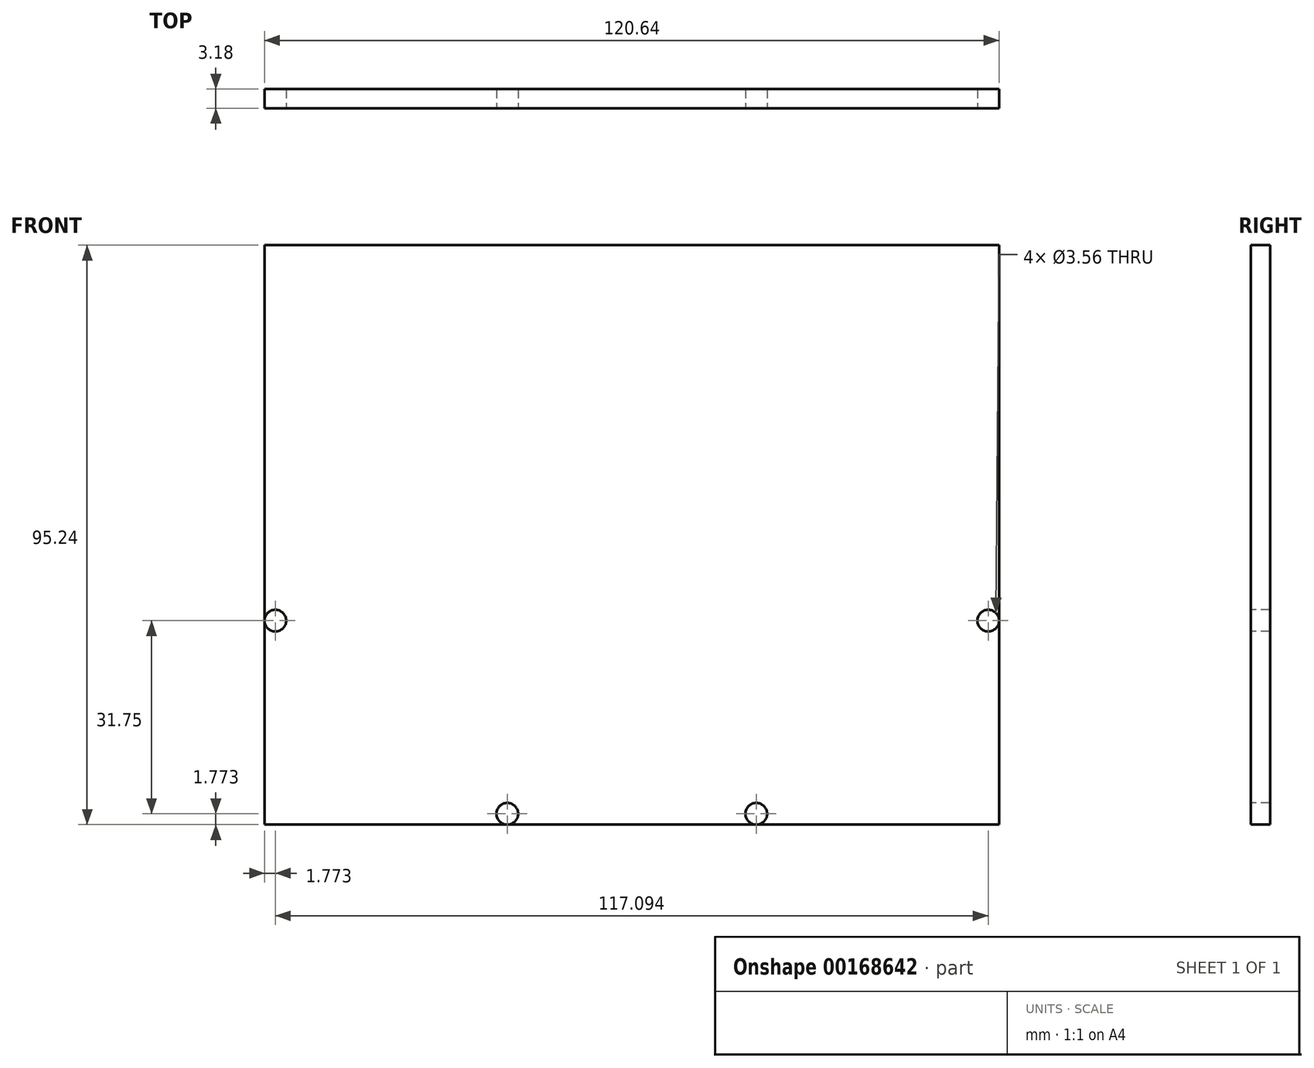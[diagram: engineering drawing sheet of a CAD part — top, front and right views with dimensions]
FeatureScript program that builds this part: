
annotation { "Feature Type Name" : "Feature", "Feature Type Description" : "" }
export const myFeature = defineFeature(function(context is Context, id is Id, definition is map)
    precondition{}
    {
        {
            var Q0;
            Q0=qCreatedBy(makeId("Front.planeOp"),FACE);
            var sketch = newSketch(context, id + "F0", { "sketchPlane" : qUnion([Q0])});
            skLineSegment(sketch, "E0.bottom", {"start": v(60.33, -47.63) * mm, "end": v(-60.33, -47.63) * mm});
            skLineSegment(sketch, "E0.top", {"start": v(60.33, 47.63) * mm, "end": v(-60.33, 47.63) * mm});
            skLineSegment(sketch, "E0.left", {"start": v(60.33, -47.63) * mm, "end": v(60.33, 47.63) * mm});
            skLineSegment(sketch, "E0.right", {"start": v(-60.33, -47.63) * mm, "end": v(-60.33, 47.62) * mm});
            skPoint(sketch, "E0.middle", {"position": v(0, 0) * mm});
            skSolve(sketch);
        }
        {
            var Q0;
            Q0=makeQuery(id+"F0.imprint","IMPRINT",FACE,{"disambiguationData":[TD([[makeQuery(id+"F0.imprint","IMPRINT",EDGE,{"derivedFrom":sQuery(id+"F0.wireOp",EDGE,"E0.bottom")}),-1.0]])]});
            extrude(context, id + "F1", {"entities" : qUnion([Q0]), "endBound" : BoundingType.SYMMETRIC, "depth" : 3.17 * mm});
        }
        {
            var Q0;
            Q0=makeQuery(id+"F1.opExtrude","CAP_FACE",FACE,{"disambiguationData":[OSD([sQuery(id+"F0.wireOp",EDGE,"E0.bottom"),sQuery(id+"F0.wireOp",EDGE,"E0.top"),sQuery(id+"F0.wireOp",EDGE,"E0.left"),sQuery(id+"F0.wireOp",EDGE,"E0.right")])],"isStart":false});
            var sketch = newSketch(context, id + "F2", { "sketchPlane" : qUnion([Q0])});
            skCircle(sketch, "E1", {"center": v(-20.45, -45.85) * mm, "radius": 1.78 * mm});
            skPoint(sketch, "E1.centerSnap0", {"position": v(0, -47.63) * mm});
            skCircle(sketch, "E2", {"center": v(-58.55, -14.1) * mm, "radius": 1.78 * mm});
            skCircle(sketch, "E3.MirrorC", {"center": v(58.55, -14.1) * mm, "radius": 1.78 * mm});
            skCircle(sketch, "E4.MirrorC", {"center": v(20.45, -45.85) * mm, "radius": 1.78 * mm});
            skSolve(sketch);
        }
        {
            var Q0;
            Q0=sQuery(id+"F2.wireOp",VERTEX,"E2.center");
            var Q1;
            Q1=sQuery(id+"F2.wireOp",VERTEX,"E1.center");
            var Q2;
            Q2=sQuery(id+"F2.wireOp",VERTEX,"E3.MirrorC.center");
            var Q3;
            Q3=sQuery(id+"F2.wireOp",VERTEX,"E4.MirrorC.center");
            var Q4;
            Q4=makeQuery(id+"F1.opExtrude","SWEPT_BODY",BODY,{"disambiguationData":[OSD([sQuery(id+"F0.wireOp",EDGE,"E0.bottom"),sQuery(id+"F0.wireOp",EDGE,"E0.top"),sQuery(id+"F0.wireOp",EDGE,"E0.left"),sQuery(id+"F0.wireOp",EDGE,"E0.right")])]});
            hole(context, id + "F3", {"style" : HoleStyle.SIMPLE, "endStyle" : HoleEndStyle.THROUGH, "holeDiameter" : 3.56 * mm, "locations" : qUnion([Q0, Q1, Q2, Q3]), "scope" : qUnion([Q4]), "isTappedThrough" : true});
        }
    });
